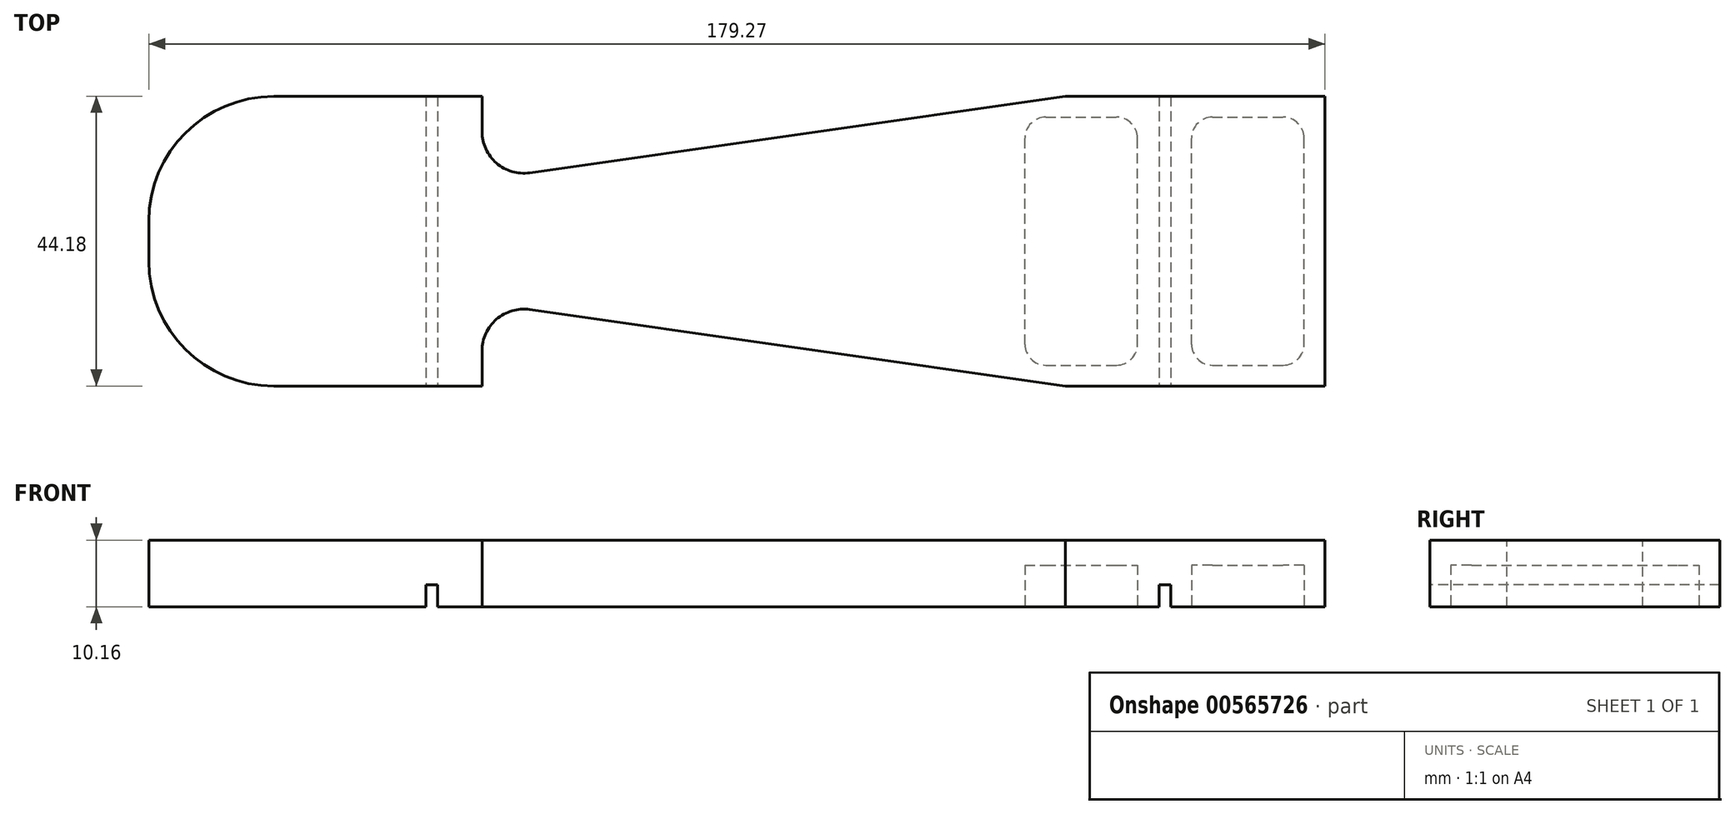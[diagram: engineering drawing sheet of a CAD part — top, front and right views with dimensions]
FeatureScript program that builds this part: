
annotation { "Feature Type Name" : "Feature", "Feature Type Description" : "" }
export const myFeature = defineFeature(function(context is Context, id is Id, definition is map)
    precondition{}
    {
        {
            var Q0;
            Q0=qCreatedBy(makeId("Front.planeOp"),FACE);
            var sketch = newSketch(context, id + "F0", { "sketchPlane" : qUnion([Q0])});
            skLineSegment(sketch, "E0.bottom", {"start": v(0, 0) * mm, "end": v(179.27, 0) * mm});
            skLineSegment(sketch, "E0.top", {"start": v(0, 31.6) * mm, "end": v(179.27, 31.6) * mm});
            skLineSegment(sketch, "E0.left", {"start": v(0, 0) * mm, "end": v(0, 31.6) * mm});
            skLineSegment(sketch, "E0.right", {"start": v(179.27, 0) * mm, "end": v(179.27, 31.6) * mm});
            skSolve(sketch);
        }
        {
            var Q0;
            Q0 = qSketchRegion(id + "F0", true);
            extrude(context, id + "F1", {"entities" : qUnion([Q0]), "endBound" : BoundingType.SYMMETRIC, "depth" : 44.17 * mm, "offsetDistance" : 25.4 * mm});
        }
        {
            var Q0;
            Q0=makeQuery(id+"F1.opExtrude","CAP_FACE",FACE,{"disambiguationData":[OSD([sQuery(id+"F0.wireOp",EDGE,"E0.bottom"),sQuery(id+"F0.wireOp",EDGE,"E0.top"),sQuery(id+"F0.wireOp",EDGE,"E0.left"),sQuery(id+"F0.wireOp",EDGE,"E0.right")])],"isStart":false});
            var sketch = newSketch(context, id + "F2", { "sketchPlane" : qUnion([Q0])});
            skLineSegment(sketch, "E1.bottom", {"start": v(42.27, 0) * mm, "end": v(44.02, 0) * mm});
            skLineSegment(sketch, "E1.top", {"start": v(42.27, 3.35) * mm, "end": v(44.02, 3.35) * mm});
            skLineSegment(sketch, "E1.left", {"start": v(42.27, 0) * mm, "end": v(42.27, 3.35) * mm});
            skLineSegment(sketch, "E1.right", {"start": v(44.02, 0) * mm, "end": v(44.02, 3.35) * mm});
            skLineSegment(sketch, "E2.bottom", {"start": v(154.03, 0) * mm, "end": v(155.78, 0) * mm});
            skLineSegment(sketch, "E2.top", {"start": v(154.03, 3.35) * mm, "end": v(155.78, 3.35) * mm});
            skLineSegment(sketch, "E2.left", {"start": v(154.03, 0) * mm, "end": v(154.03, 3.35) * mm});
            skLineSegment(sketch, "E2.right", {"start": v(155.78, 0) * mm, "end": v(155.78, 3.35) * mm});
            skSolve(sketch);
        }
        {
            var Q0;
            Q0 = qSketchRegion(id + "F2", true);
            extrude(context, id + "F3", {"entities" : qUnion([Q0]), "operationType" : NewBodyOperationType.REMOVE, "endBound" : BoundingType.THROUGH_ALL, "oppositeDirection" : true, "depth" : 25.4 * mm, "offsetDistance" : 25.4 * mm});
        }
        {
            var Q0;
            Q0=makeQuery(id+"F1.opExtrude","CAP_FACE",FACE,{"disambiguationData":[OSD([sQuery(id+"F0.wireOp",EDGE,"E0.bottom"),sQuery(id+"F0.wireOp",EDGE,"E0.top"),sQuery(id+"F0.wireOp",EDGE,"E0.left"),sQuery(id+"F0.wireOp",EDGE,"E0.right")])],"isStart":false});
            var sketch = newSketch(context, id + "F4", { "sketchPlane" : qUnion([Q0])});
            skLineSegment(sketch, "E3.bottom", {"start": v(0, 31.6) * mm, "end": v(179.27, 31.6) * mm});
            skLineSegment(sketch, "E3.top", {"start": v(0, 10.16) * mm, "end": v(179.27, 10.16) * mm});
            skLineSegment(sketch, "E3.left", {"start": v(0, 31.6) * mm, "end": v(0, 10.16) * mm});
            skLineSegment(sketch, "E3.right", {"start": v(179.27, 31.6) * mm, "end": v(179.27, 10.16) * mm});
            skSolve(sketch);
        }
        {
            var Q0;
            Q0 = qSketchRegion(id + "F4", true);
            extrude(context, id + "F5", {"entities" : qUnion([Q0]), "operationType" : NewBodyOperationType.REMOVE, "endBound" : BoundingType.THROUGH_ALL, "oppositeDirection" : true, "depth" : 25.4 * mm, "offsetDistance" : 25.4 * mm});
        }
        {
            var Q0;
            Q0=makeQuery(id+"F5.boolean.opBoolean","COPY",FACE,{"derivedFrom":makeQuery(id+"F5.opExtrude","SWEPT_FACE",FACE,{"disambiguationData":[OSD([sQuery(id+"F4.wireOp",EDGE,"E3.top")])]})});
            var sketch = newSketch(context, id + "F6", { "sketchPlane" : qUnion([Q0])});
            skLineSegment(sketch, "E4", {"start": v(139.7, 22.09) * mm, "end": v(58.05, 10.42) * mm});
            skLineSegment(sketch, "E5", {"start": v(50.8, 16.7) * mm, "end": v(50.8, 22.09) * mm});
            skLineSegment(sketch, "E6", {"start": v(139.7, 22.09) * mm, "end": v(50.8, 22.09) * mm});
            skLineSegment(sketch, "E7", {"start": v(58.05, -10.42) * mm, "end": v(139.7, -22.09) * mm});
            skLineSegment(sketch, "E8", {"start": v(50.8, -16.7) * mm, "end": v(50.8, -22.09) * mm});
            skLineSegment(sketch, "E9", {"start": v(139.7, -22.09) * mm, "end": v(50.8, -22.09) * mm});
            skPoint(sketch, "E10.visualSharp", {"position": v(50.8, 9.39) * mm});
            skArc(sketch, "E10.filletArc", {"start": v(50.8, 16.7) * mm, "mid": v(52.99, 11.9) * mm, "end": v(58.05, 10.42) * mm});
            skPoint(sketch, "E11.visualSharp", {"position": v(50.8, -9.39) * mm});
            skArc(sketch, "E11.filletArc", {"start": v(58.05, -10.42) * mm, "mid": v(52.99, -11.9) * mm, "end": v(50.8, -16.7) * mm});
            skSolve(sketch);
        }
        {
            var Q0;
            Q0 = qSketchRegion(id + "F6", true);
            extrude(context, id + "F7", {"entities" : qUnion([Q0]), "operationType" : NewBodyOperationType.REMOVE, "endBound" : BoundingType.THROUGH_ALL, "oppositeDirection" : true, "depth" : 25.4 * mm, "offsetDistance" : 25.4 * mm});
        }
        {
            var Q0;
            {var subQ0=sQuery(id+"F0.wireOp",EDGE,"E0.right");var subQ3=sQuery(id+"F0.wireOp",EDGE,"E0.bottom");Q0=makeQuery(id+"F3.boolean.opBoolean","SPLIT",FACE,{"disambiguationData":[TD([makeQuery(id+"F1.opExtrude","SWEPT_FACE",FACE,{"disambiguationData":[OSD([subQ0])]})])],"derivedFrom":makeQuery(id+"F1.opExtrude","SWEPT_FACE",FACE,{"disambiguationData":[OSD([subQ3])]})});}
            var sketch = newSketch(context, id + "F8", { "sketchPlane" : qUnion([Q0])});
            skLineSegment(sketch, "E12.bottom", {"start": v(162.13, 18.91) * mm, "end": v(172.92, 18.91) * mm});
            skLineSegment(sketch, "E12.top", {"start": v(162.13, -18.91) * mm, "end": v(172.92, -18.91) * mm});
            skLineSegment(sketch, "E12.left", {"start": v(158.95, 15.74) * mm, "end": v(158.95, -15.74) * mm});
            skLineSegment(sketch, "E12.right", {"start": v(176.1, 15.74) * mm, "end": v(176.1, -15.74) * mm});
            skLineSegment(sketch, "E13.bottom", {"start": v(136.73, 18.91) * mm, "end": v(147.52, 18.91) * mm});
            skLineSegment(sketch, "E13.top", {"start": v(136.73, -18.91) * mm, "end": v(147.52, -18.91) * mm});
            skLineSegment(sketch, "E13.left", {"start": v(133.55, 15.74) * mm, "end": v(133.55, -15.74) * mm});
            skLineSegment(sketch, "E13.right", {"start": v(150.7, 15.74) * mm, "end": v(150.7, -15.74) * mm});
            skPoint(sketch, "E14.visualSharp", {"position": v(133.55, 18.91) * mm});
            skArc(sketch, "E14.filletArc", {"start": v(136.73, 18.91) * mm, "mid": v(134.48, 17.98) * mm, "end": v(133.55, 15.74) * mm});
            skPoint(sketch, "E15.visualSharp", {"position": v(133.55, -18.91) * mm});
            skArc(sketch, "E15.filletArc", {"start": v(133.55, -15.74) * mm, "mid": v(134.48, -17.98) * mm, "end": v(136.73, -18.91) * mm});
            skPoint(sketch, "E16.visualSharp", {"position": v(150.7, -18.91) * mm});
            skArc(sketch, "E16.filletArc", {"start": v(147.52, -18.91) * mm, "mid": v(149.77, -17.98) * mm, "end": v(150.7, -15.74) * mm});
            skPoint(sketch, "E17.visualSharp", {"position": v(150.7, 18.91) * mm});
            skArc(sketch, "E17.filletArc", {"start": v(150.7, 15.74) * mm, "mid": v(149.77, 17.98) * mm, "end": v(147.52, 18.91) * mm});
            skPoint(sketch, "E18.visualSharp", {"position": v(158.95, 18.91) * mm});
            skArc(sketch, "E18.filletArc", {"start": v(162.13, 18.91) * mm, "mid": v(159.88, 17.98) * mm, "end": v(158.95, 15.74) * mm});
            skPoint(sketch, "E19.visualSharp", {"position": v(176.1, 18.91) * mm});
            skArc(sketch, "E19.filletArc", {"start": v(176.1, 15.74) * mm, "mid": v(175.17, 17.98) * mm, "end": v(172.92, 18.91) * mm});
            skPoint(sketch, "E20.visualSharp", {"position": v(176.1, -18.91) * mm});
            skArc(sketch, "E20.filletArc", {"start": v(172.92, -18.91) * mm, "mid": v(175.17, -17.98) * mm, "end": v(176.1, -15.74) * mm});
            skPoint(sketch, "E21.visualSharp", {"position": v(158.95, -18.91) * mm});
            skArc(sketch, "E21.filletArc", {"start": v(158.95, -15.74) * mm, "mid": v(159.88, -17.98) * mm, "end": v(162.13, -18.91) * mm});
            skSolve(sketch);
        }
        {
            var Q0;
            Q0 = qSketchRegion(id + "F8", true);
            extrude(context, id + "F9", {"entities" : qUnion([Q0]), "operationType" : NewBodyOperationType.REMOVE, "oppositeDirection" : true, "depth" : 6.35 * mm, "offsetDistance" : 25.4 * mm});
        }
        {
            var Q0;
            Q0=makeQuery(id+"F5.boolean.opBoolean","COPY",FACE,{"derivedFrom":makeQuery(id+"F5.opExtrude","SWEPT_FACE",FACE,{"disambiguationData":[OSD([sQuery(id+"F4.wireOp",EDGE,"E3.top")])]})});
            var sketch = newSketch(context, id + "F10", { "sketchPlane" : qUnion([Q0])});
            skLineSegment(sketch, "E22", {"start": v(19.05, 22.09) * mm, "end": v(0, 22.09) * mm});
            skLineSegment(sketch, "E23", {"start": v(0, 22.09) * mm, "end": v(0, 3.04) * mm});
            skLineSegment(sketch, "E24", {"start": v(0, -3.04) * mm, "end": v(0, -22.09) * mm});
            skLineSegment(sketch, "E25", {"start": v(0, -22.09) * mm, "end": v(19.05, -22.09) * mm});
            skArc(sketch, "E26", {"start": v(19.05, 22.09) * mm, "mid": v(5.58, 16.5) * mm, "end": v(0, 3.04) * mm});
            skArc(sketch, "E27", {"start": v(0, -3.04) * mm, "mid": v(5.58, -16.5) * mm, "end": v(19.05, -22.09) * mm});
            skSolve(sketch);
        }
        {
            var Q0;
            Q0 = qSketchRegion(id + "F10", true);
            extrude(context, id + "F11", {"entities" : qUnion([Q0]), "operationType" : NewBodyOperationType.REMOVE, "endBound" : BoundingType.THROUGH_ALL, "oppositeDirection" : true, "depth" : 25.4 * mm, "offsetDistance" : 25.4 * mm});
        }
    });
